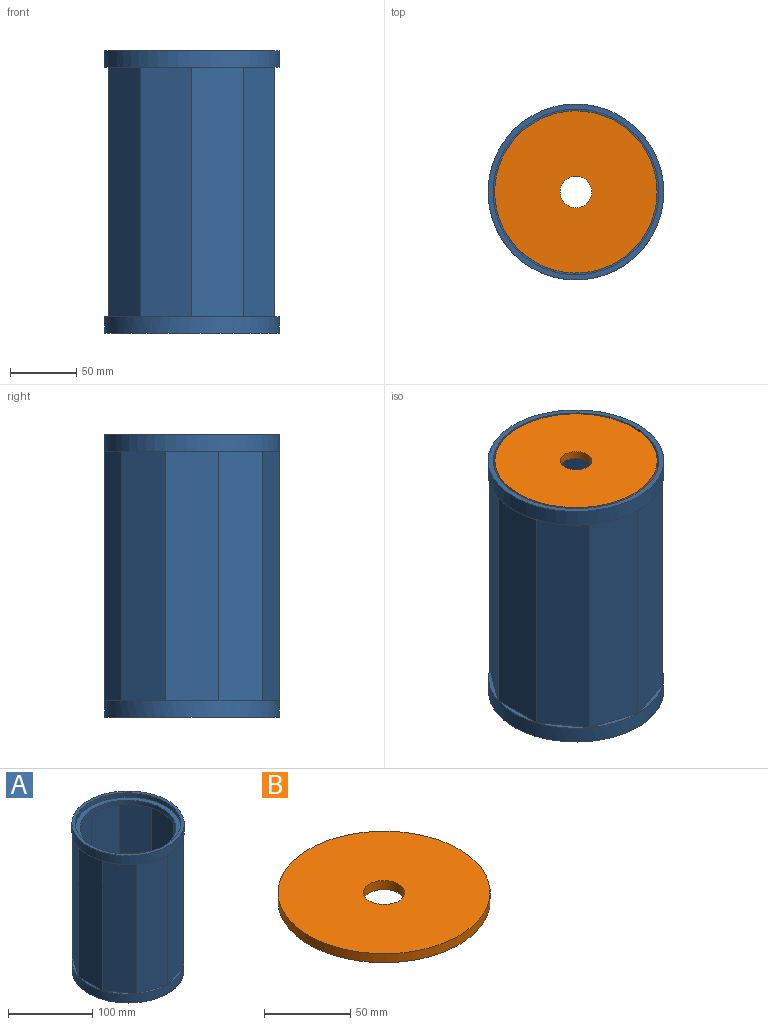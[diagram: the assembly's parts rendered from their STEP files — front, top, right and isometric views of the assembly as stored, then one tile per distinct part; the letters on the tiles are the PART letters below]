
ASSEMBLY  parts=2 mates=1
PART A: 32 faces, bbox 132.9x132.9x213.6 mm
  f0: plane 121.78x115.82mm, normal (0,0,-1), area 841.5mm2, adj f2,f3,f4,f5,f6,f7,f8,f9
  f1: plane 121.78x115.82mm, normal (0,0,1), area 10411.1mm2, adj f2,f3,f4,f5,f6,f7,f8,f9
  f2: plane 188.21x35.79mm, normal (0.31,-0.95,0), area 7083.2mm2, adj f0,f1,f3,f11
  f3: plane 188.21x30.45mm, normal (0.81,-0.59,0), area 7083.2mm2, adj f0,f1,f2,f4
  f4: plane 188.21x37.63mm, normal (1,0,0), area 7083.2mm2, adj f0,f1,f3,f5
  f5: plane 188.21x30.45mm, normal (0.81,0.59,0), area 7083.2mm2, adj f0,f1,f4,f6
  f6: plane 188.21x35.79mm, normal (0.31,0.95,0), area 7083.2mm2, adj f0,f1,f5,f7
  f7: plane 188.21x35.79mm, normal (-0.31,0.95,0), area 7083.2mm2, adj f0,f1,f6,f8
  f8: plane 188.21x30.45mm, normal (-0.81,0.59,0), area 7083.2mm2, adj f0,f1,f7,f9
  f9: plane 188.21x37.63mm, normal (-1,0,0), area 7083.2mm2, adj f0,f1,f8,f10
  f10: plane 188.21x30.45mm, normal (-0.81,-0.59,0), area 7083.2mm2, adj f0,f1,f9,f11
  f11: plane 188.21x35.79mm, normal (-0.31,-0.95,0), area 7083.2mm2, adj f0,f1,f2,f10
  f12: cylinder r=56.58mm len=113.15mm, axis (0,0,1), area 2257.3mm2, adj f0,f30
  f13: plane 188.21x33.01mm, normal (0.81,0.59,0), area 7679.6mm2, adj f14,f22,f25,f28
  f14: plane 188.21x38.81mm, normal (0.31,0.95,0), area 7679.6mm2, adj f13,f15,f25,f28
  f15: plane 188.21x38.81mm, normal (-0.31,0.95,0), area 7679.6mm2, adj f14,f16,f25,f28
  f16: plane 188.21x33.01mm, normal (-0.81,0.59,0), area 7679.6mm2, adj f15,f17,f25,f28
  f17: plane 188.21x40.8mm, normal (-1,0,0), area 7679.6mm2, adj f16,f18,f25,f28
  f18: plane 188.21x33.01mm, normal (-0.81,-0.59,0), area 7679.6mm2, adj f17,f19,f25,f28
  f19: plane 188.21x38.81mm, normal (-0.31,-0.95,0), area 7679.6mm2, adj f18,f20,f25,f28
  f20: plane 188.21x38.81mm, normal (0.31,-0.95,0), area 7679.6mm2, adj f19,f21,f25,f28
  f21: plane 188.21x33.01mm, normal (0.81,-0.59,0), area 7679.6mm2, adj f20,f22,f25,f28
  f22: plane 188.21x40.8mm, normal (1,0,0), area 7679.6mm2, adj f13,f21,f25,f28
  f23: cylinder r=66.14mm len=132.29mm, axis (0,0,1), area 5278mm2, adj f24,f25
  f24: plane 132.29x132.29mm, normal (0,0,-1), area 13258.2mm2, adj f23,f31
  f25: plane 132.29x132.29mm, normal (0,0,1), area 934.5mm2, adj f13,f14,f15,f16,f17,f18,f19,f20
  f26: cylinder r=66.45mm len=132.91mm, axis (0,0,-1), area 5302.9mm2, adj f27,f28
  f27: plane 132.91x132.91mm, normal (0,0,1), area 1574.9mm2, adj f26,f29
  f28: plane 132.91x132.91mm, normal (0,0,-1), area 1064.4mm2, adj f13,f14,f15,f16,f17,f18,f19,f20
  f29: cylinder r=62.57mm len=125.14mm, axis (0,0,-1), area 2496.4mm2, adj f27,f30
  f30: plane 125.14x125.14mm, normal (0,0,1), area 2243.6mm2, adj f12,f29
  f31: cylinder r=12.44mm len=24.88mm, axis (0,0,1), area 992.5mm2, adj f1,f24
PART B: 4 faces, bbox 122.7x122.7x6.4 mm
  f0: cylinder r=61.33mm len=122.66mm, axis (0,0,-1), area 2446.9mm2, adj f1,f2
  f1: plane 122.66x122.66mm, normal (0,0,1), area 11366.6mm2, adj f0,f3
  f2: plane 122.66x122.66mm, normal (0,0,-1), area 11366.6mm2, adj f0,f3
  f3: cylinder r=11.96mm len=23.92mm, axis (0,0,-1), area 477.3mm2, adj f1,f2
PLACE A t=(-0.68,-1.03,-0.96)mm fixed
PLACE B t=(-0.68,-1.03,-0.96)mm
MATE fastened B.f0 <-> A.f12  axis (0,0,-1) through (-0.68,-1.03,-0.96)mm
